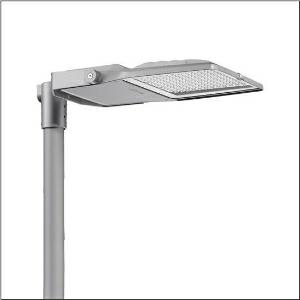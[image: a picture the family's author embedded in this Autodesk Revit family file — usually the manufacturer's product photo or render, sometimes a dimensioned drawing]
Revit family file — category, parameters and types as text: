
# Revit family: floodlight_fl_21_midi___pl61_5xa7786e4c3a_509f
name_source: partatom
category: Lighting Fixtures
units: mm (PartAtom-declared; Revit-internal decimal feet)

## family parameters
Cut with Voids When Loaded = No
Host = Face
Light Source = No
Part Type = Normal
Room Calculation Point = No
Round Connector Dimension = Use Diameter
Shared = No

## types (1)
- --- (1 x LED, 27590 lm, 212.4 W, 4000K)
    Apparent Load = 212 VA
    CIE Flux Codes = 33 65 98 100 100
    Color Rendering = 70
    Color Temperature = 4000K
    Default Elevation = 1800 mm
    Description = Floodlight FL 21 midi, floodlight, primary light control with lens, of PMMA, primary optical cover: protective disc, of toughened safety glass, transparent, light distribution: PL61, light emission: direct distribution, installation type: surface-mounted, LED, High Power LED, rated luminous flux: 27.590lm, luminous efficacy: 130lm/W, light colour: 740, colour temperature: 4000K, control gear: Smart Interface (Zhaga)D4i, control: overheat protection, constant luminous flux control, time-dependent luminous flux control, flexible luminous flux parameterisation, pre-setting: logarithmic dimming characteristic, with terminal, 6-pole, mains connection: 220..240V, AC, 50/60Hz, start of lifetime: 212W, end of service life: 231W, reduction: 95W, mast bracket, of diecast aluminium, powder-coated, SITECO metallic grey (DB 702S), corrosivity category C5 mid according to DIN EN ISO 12944, suitable for swimming pools, chlorine-resistant, sealing non-destructively replaceable, mast bracket, of steel, galvanised, powder-coated, SITECO metallic grey (DB 702S), Smart Interface below and above, protection rating (complete): IP66, insulation class (complete): insulation class II (safety insulation), certification: CE, ENEC, VDE, protection symbol: D, impact resistance: IK08, permissible operating ambient temperature: -40..+40°C, permissible operating ambient temperature for outdoor applications: -40..+50°C, standard: DIN EN 12944, LABS conformity tested according to VDMA 24364:2018-05, packaging unit: 1 piece

Light Distribution: PL61
    Height = 76 mm
    Lamp = 1 x LED
    Lamp Light Flux = 27590 lm
    Lamp Power = 212.4 W
    Lamp count = 1
    Length = 657 mm
    Luminous efficacy = 130 lm/W
    Manufacturer = Siteco
    ModVariant = No
    Model = 5XA7786E4C3A
    Number of Poles = 1
    OnlyDefault = Yes
    Power Factor = 1
    Product Name = Floodlight FL 21 midi | PL61
    Product group = floodlight | pylon annexe
    ProductGroupID = 6201
    Protection Class = Protection class II
    Protection Degree = IP 66
    RLX_Detail_Level = 1
    RLX_Emergency_Light_Flux = 0 lm
    RLX_Emergency_Type = 0
    RLX_Emergency_Type_DB = No
    RlxData = <blob elided: 104773 chars, md5=0d6a7b50>
    Socket = socket
    Standby Power = 0 W
    System Light Flux = 27590 lm
    System Power = 212 W
    Type Comments = factory setting: luminous flux: 100 % | dim-lin: 254 | 710 mA
    Type Image = l_1007123.jpg
    URL = http://relux.com
    VarID = @adj_094359
    Voltage = 0 V
    Weight = 0.00 kg
    Width = 442 mm

## geometry (parser evidence)
native form markers: Blend x4, Sweep x10
no freeform markers — native parametric forms only
